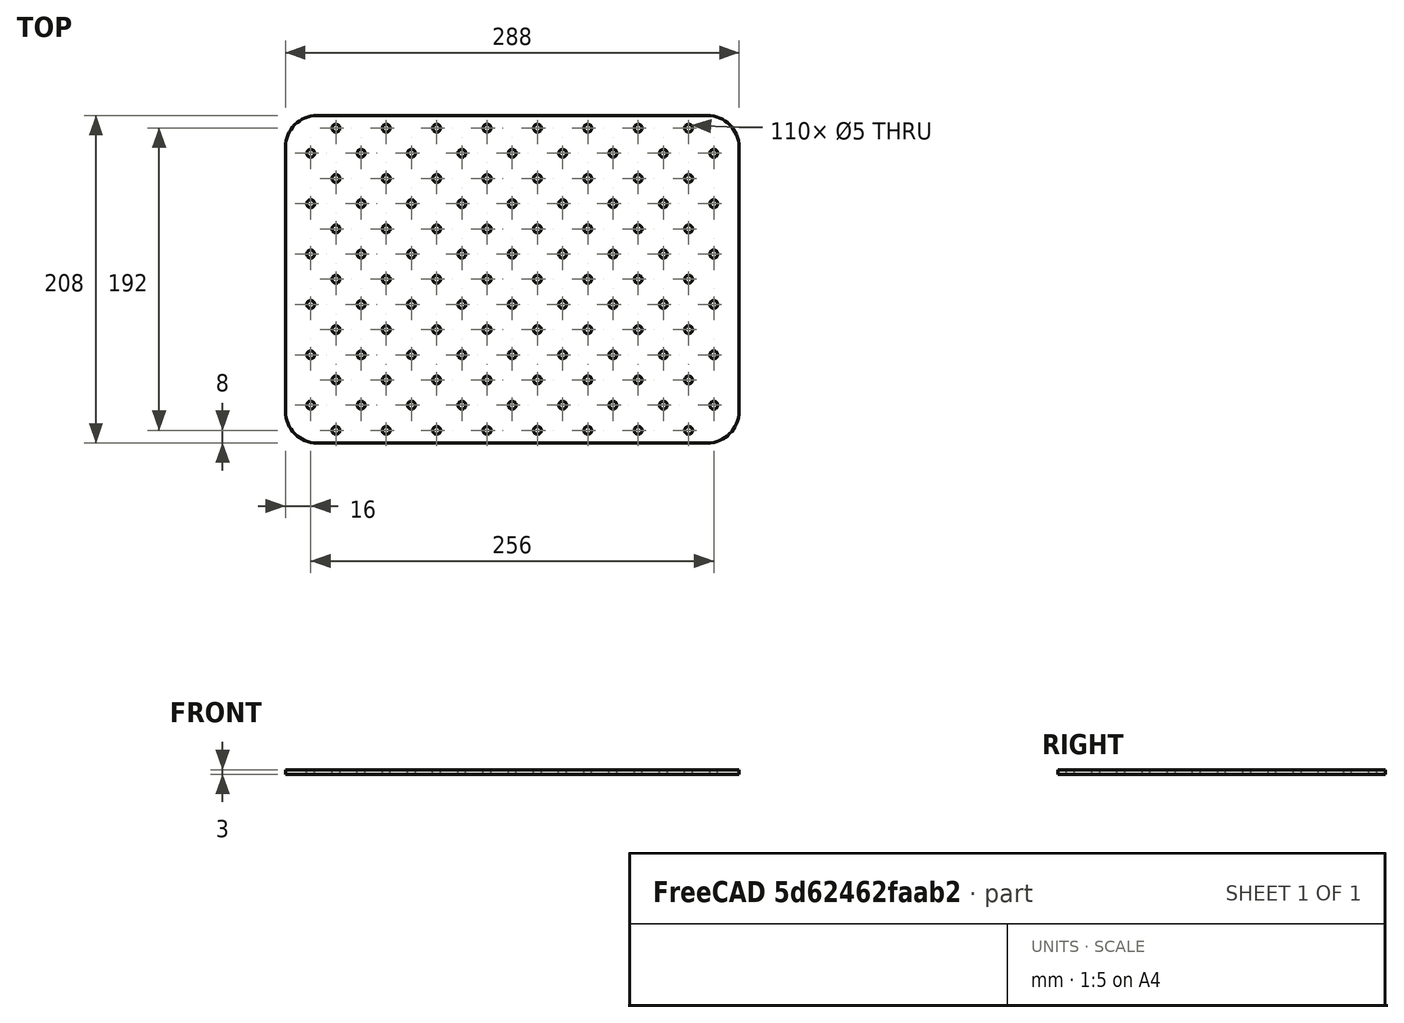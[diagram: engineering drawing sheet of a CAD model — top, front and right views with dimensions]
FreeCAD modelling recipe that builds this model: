
FCSTD DOCUMENT  (FreeCAD 0.21R33771 (Git))
Label: 32-grid-Base-Plate+16mm
License: All rights reserved
LicenseURL: http://en.wikipedia.org/wiki/All_rights_reserved
objects: TechDraw::DrawViewDimension×10, PartDesign::LinearPattern×4, Sketcher::SketchObject×3, TechDraw::DrawProjGroupItem×3, PartDesign::Hole×2, PartDesign::MultiTransform×2, TechDraw::DrawSVGTemplate×2, TechDraw::DrawPage×2, App::TextDocument×1, Spreadsheet::Sheet×1, PartDesign::Pad×1, TechDraw::DrawViewAnnotation×1, PartDesign::Body×1, TechDraw::DrawViewPart×1, TechDraw::DrawProjGroup×1, TechDraw::DrawViewBalloon×1
note: 34 computed .brp shape members not serialized (recipe doc carries the construction recipe); baked Part::Feature solids carry a one-line shape summary decoded from their .brp

FEATURE [Sketcher::SketchObject] Sketch  label="main-base-sketch"
  FullyConstrained = true
  MapMode = 5
  Support = -> [XY_Plane]
  expr: Constraints[16] = Spreadsheet.base_grid * Spreadsheet.vertical + Spreadsheet.extra_space
  expr: Constraints[17] = Spreadsheet.base_grid * Spreadsheet.horizontal
  expr: Constraints[18] = Spreadsheet.corner_rad
  sketch-geometry (8):
    g0: LineSegment StartX=-124 StartY=104 StartZ=0 EndX=124 EndY=104 EndZ=0
    g1: LineSegment StartX=144 StartY=84 StartZ=0 EndX=144 EndY=-84 EndZ=0
    g2: LineSegment StartX=124 StartY=-104 StartZ=0 EndX=-124 EndY=-104 EndZ=0
    g3: LineSegment StartX=-144 StartY=-84 StartZ=0 EndX=-144 EndY=84 EndZ=0
    g4: ArcOfCircle CenterX=124 CenterY=-84 CenterZ=0 NormalX=0 NormalY=0 NormalZ=1 AngleXU=0 Radius=20 StartAngle=4.71239 EndAngle=6.28319
    g5: ArcOfCircle CenterX=-124 CenterY=84 CenterZ=0 NormalX=0 NormalY=0 NormalZ=1 AngleXU=0 Radius=20 StartAngle=1.5708 EndAngle=3.14159
    g6: ArcOfCircle CenterX=124 CenterY=84 CenterZ=0 NormalX=0 NormalY=0 NormalZ=1 AngleXU=0 Radius=20 StartAngle=7e-16 EndAngle=1.5708
    g7: ArcOfCircle CenterX=-124 CenterY=-84 CenterZ=0 NormalX=0 NormalY=0 NormalZ=1 AngleXU=0 Radius=20 StartAngle=3.14159 EndAngle=4.71239
  constraints (19):
    c: Horizontal(g0)
    c: Horizontal(g2)
    c: Vertical(g1)
    c: Vertical(g3)
    c: Tangent(g1,g4) = 1.5708
    c: Tangent(g2,g4) = 1.5708
    c: Tangent(g3,g5) = 1.5708
    c: Tangent(g0,g5) = 1.5708
    c: Tangent(g0,g6) = 1.5708
    c: Tangent(g1,g6) = 1.5708
    c: Tangent(g3,g7) = 1.5708
    c: Tangent(g2,g7) = 1.5708
    c: Equal(g6,g4)
    c: Equal(g4,g7)
    c: Equal(g7,g5)
    c: Symmetric(g4,g5,g-1)
    c: DistanceY(g2,g0) = 208
    c: DistanceX(g3,g1) = 288
    c: Radius(g6) = 20
FEATURE [App::TextDocument] Text_document  label="notes"
  Text = 32mm+16mm Offset Double-Grid to be later transferred into different parametric options
FEATURE [Spreadsheet::Sheet] Spreadsheet  label="Parameters"
  cells = A1='Ref; B1='Value; C1='Description; A2='grid_boring; B2(grid_boring)=5; C2='main bore holes reference for grid; A3='corner_rad; B3(corner_rad)=20; C3='radius of the base plate corners; A4='base_grid; B4(base_grid)=32; C4='grid standard reference (standard 32mm); A5='thickness; B5(thickness)=3; C5='base plate thickness of material; A6='horizontal; B6(horizontal)=9; C6='holes horizonal; A7='vertical; B7(vertical)=6; C7='holes vertical; A8='grid_factor; B8(grid_factor)=1; C8='change the base grid reference for parametric designs; A9='extra_space; B9(extra_space)=16; C9='Extra Space vertically (Standard 0, Variant 16mm)
FEATURE [PartDesign::Pad] Pad
  Direction = (0,0,1)
  Length = 3
  Length2 = 10
  Profile = -> Sketch
  ReferenceAxis = -> Sketch [N_Axis]
  Type = 0
  expr: Length = Spreadsheet.thickness
FEATURE [Sketcher::SketchObject] Sketch001  label="bore-hole-sketch"
  FullyConstrained = true
  MapMode = 5
  Support = -> [XY_Plane]
  expr: Constraints[16] = Sketch.Constraints[16]
  expr: Constraints[17] = Sketch.Constraints[17]
  expr: Constraints[18] = Sketch.Constraints[18]
  expr: Constraints[19] = Spreadsheet.base_grid * Spreadsheet.grid_factor / 2 + Spreadsheet.extra_space / 2
  expr: Constraints[20] = Spreadsheet.base_grid * Spreadsheet.grid_factor / 2
  expr: Constraints[21] = Spreadsheet.grid_boring
  sketch-geometry (9):
    g0: LineSegment StartX=-124 StartY=104 StartZ=0 EndX=124 EndY=104 EndZ=0
    g1: LineSegment StartX=144 StartY=84 StartZ=0 EndX=144 EndY=-84 EndZ=0
    g2: LineSegment StartX=124 StartY=-104 StartZ=0 EndX=-124 EndY=-104 EndZ=0
    g3: LineSegment StartX=-144 StartY=-84 StartZ=0 EndX=-144 EndY=84 EndZ=0
    g4: ArcOfCircle CenterX=124 CenterY=-84 CenterZ=0 NormalX=0 NormalY=0 NormalZ=1 AngleXU=0 Radius=20 StartAngle=4.71239 EndAngle=6.28319
    g5: ArcOfCircle CenterX=-124 CenterY=84 CenterZ=0 NormalX=0 NormalY=0 NormalZ=1 AngleXU=0 Radius=20 StartAngle=1.5708 EndAngle=3.14159
    g6: ArcOfCircle CenterX=124 CenterY=84 CenterZ=0 NormalX=0 NormalY=0 NormalZ=1 AngleXU=0 Radius=20 StartAngle=2e-16 EndAngle=1.5708
    g7: ArcOfCircle CenterX=-124 CenterY=-84 CenterZ=0 NormalX=0 NormalY=0 NormalZ=1 AngleXU=0 Radius=20 StartAngle=3.14159 EndAngle=4.71239
    g8: Circle CenterX=128 CenterY=80 CenterZ=0 NormalX=0 NormalY=0 NormalZ=1 AngleXU=0 Radius=2.5
  constraints (22):
    c: Horizontal(g0)
    c: Horizontal(g2)
    c: Vertical(g1)
    c: Vertical(g3)
    c: Tangent(g1,g4) = 1.5708
    c: Tangent(g2,g4) = 1.5708
    c: Tangent(g3,g5) = 1.5708
    c: Tangent(g0,g5) = 1.5708
    c: Tangent(g0,g6) = 1.5708
    c: Tangent(g1,g6) = 1.5708
    c: Tangent(g3,g7) = 1.5708
    c: Tangent(g2,g7) = 1.5708
    c: Equal(g6,g4)
    c: Equal(g4,g7)
    c: Equal(g7,g5)
    c: Symmetric(g4,g5,g-1)
    c: DistanceY(g2,g0) = 208
    c: DistanceX(g3,g1) = 288
    c: Radius(g6) = 20
    c: DistanceY(g8,g0) = 24
    c: DistanceX(g8,g1) = 16
    c: Diameter(g8) = 5
FEATURE [PartDesign::Hole] Hole  label="Base-Bore-Hole"
  BaseFeature = -> Pad
  CustomThreadClearance = 0
  Depth = 699.261
  DepthType = 1
  Diameter = 5
  DrillForDepth = false
  DrillPoint = 1
  DrillPointAngle = 118
  HoleCutCountersinkAngle = 90
  HoleCutCustomValues = false
  HoleCutDepth = 0
  HoleCutDiameter = 6.1
  HoleCutType = 0
  ModelThread = false
  Profile = -> Sketch001
  Reversed = true
  Tapered = false
  TaperedAngle = 90
  ThreadClass = 0
  ThreadDepth = 699.261
  ThreadDepthType = 0
  ThreadDirection = 0
  ThreadFit = 0
  ThreadSize = 0
  ThreadType = 0
  Threaded = false
  UseCustomThreadClearance = false
  expr: Diameter = Spreadsheet.grid_boring
FEATURE [PartDesign::LinearPattern] LinearPattern
  Direction = -> Sketch001 [H_Axis]
  Length = 256
  Occurrences = 9
  Reversed = true
  expr: Length = Spreadsheet.base_grid * Spreadsheet.grid_factor * (Spreadsheet.horizontal / Spreadsheet.grid_factor - 1)
  expr: Occurrences = Spreadsheet.horizontal / Spreadsheet.grid_factor
FEATURE [PartDesign::LinearPattern] LinearPattern001
  Direction = -> Sketch001 [V_Axis]
  Length = 160
  Occurrences = 6
  Reversed = true
  expr: Length = Spreadsheet.base_grid * Spreadsheet.grid_factor * (Spreadsheet.vertical / Spreadsheet.grid_factor - 1)
  expr: Occurrences = Spreadsheet.vertical / Spreadsheet.grid_factor
FEATURE [PartDesign::MultiTransform] MultiTransform  label="Base-Grid-Bore-Holes"
  BaseFeature = -> Hole
  Originals = -> [Hole]
  Transformations = -> [LinearPattern,LinearPattern001]
FEATURE [TechDraw::DrawSVGTemplate] Template001  label="Base Plate Page1"
  EditableTexts = AUTHOR_NAME=Timm Wille; DRAWING_TITLE=32mmx2 (+16mm) Grid Base Plate; FC-DATE=16.10.2024; FC-REV=v0.2-1; FC-SC=1/2; FC-SH=1 / 1; FC-SI=A3; FreeCAD_DRAWING=FreeCAD DRAWING; SI-1=in mm; SI-6=LICENSE: CC-BY-SA 4.0
  Height = 297
  Orientation = 1
  Template = <path>
  Width = 420
FEATURE [TechDraw::DrawSVGTemplate] Template
  Height = 297
  Orientation = 1
  Template = <path>
  Width = 420
FEATURE [Sketcher::SketchObject] Sketch002  label="secondary-grid-bore-hole"
  ExternalGeometry = -> [Sketch001,Sketch]
  FullyConstrained = true
  MapMode = 5
  Support = -> [XY_Plane]
  expr: Constraints[0] = Spreadsheet.base_grid / 2
  expr: Constraints[1] = Spreadsheet.base_grid / 2
  expr: Constraints[2] = Spreadsheet.grid_boring
  sketch-geometry (1):
    g0: Circle CenterX=112 CenterY=96 CenterZ=0 NormalX=0 NormalY=0 NormalZ=1 AngleXU=0 Radius=2.5
  constraints (3):
    c: DistanceX(g0,g-3) = 16
    c: DistanceY(g-3,g0) = 16
    c: Diameter(g0) = 5
FEATURE [TechDraw::DrawViewAnnotation] Annotation
  Font = osifont
  LineSpace = 100
  LockPosition = false
  MaxWidth = -1
  Rotation = 0
  ScaleType = 0
  Text = Technical Drawing of the #ASKotec Modules Base Plate | 2x 32x32mm grid paddern (shift 16mm) for Prototyping | packing and collections setups
  TextSize = 5
  TextStyle = 0
  X = 120.347
  Y = 202.608
FEATURE [PartDesign::Hole] Hole001  label="Secondary-Bore-Hole"
  BaseFeature = -> MultiTransform
  CustomThreadClearance = 0
  Depth = 717.646
  DepthType = 1
  Diameter = 5
  DrillForDepth = false
  DrillPoint = 1
  DrillPointAngle = 118
  HoleCutCountersinkAngle = 90
  HoleCutCustomValues = false
  HoleCutDepth = 0
  HoleCutDiameter = 6.1
  HoleCutType = 0
  ModelThread = false
  Profile = -> Sketch002
  Reversed = true
  Tapered = false
  TaperedAngle = 90
  ThreadClass = 0
  ThreadDepth = 717.646
  ThreadDepthType = 0
  ThreadDirection = 0
  ThreadFit = 0
  ThreadSize = 0
  ThreadType = 0
  Threaded = false
  UseCustomThreadClearance = false
  expr: Diameter = Spreadsheet.grid_boring
FEATURE [PartDesign::LinearPattern] LinearPattern002
  Direction = -> Sketch002 [H_Axis]
  Length = 224
  Occurrences = 8
  Reversed = true
  expr: Length = Spreadsheet.base_grid * Spreadsheet.grid_factor * (Spreadsheet.horizontal / Spreadsheet.grid_factor - 2)
  expr: Occurrences = Spreadsheet.horizontal - 1
FEATURE [PartDesign::LinearPattern] LinearPattern003
  Direction = -> Sketch002 [V_Axis]
  Length = 192
  Occurrences = 7
  Reversed = true
  expr: Length = Spreadsheet.base_grid * Spreadsheet.grid_factor * Spreadsheet.vertical / Spreadsheet.grid_factor
  expr: Occurrences = Spreadsheet.vertical + 1
FEATURE [PartDesign::MultiTransform] MultiTransform001  label="Secondary-Grid-Bore-Holes"
  BaseFeature = -> Hole001
  Originals = -> [Hole001]
  Transformations = -> [LinearPattern002,LinearPattern003]
FEATURE [PartDesign::Body] Body  label="Base-Plate"
  Group = -> [Sketch,Pad,Sketch001,Hole,MultiTransform,LinearPattern,LinearPattern001,Sketch002,Hole001,MultiTransform001,LinearPattern002,LinearPattern003]
  Origin = -> Origin
  Tip = -> MultiTransform001
FEATURE [TechDraw::DrawProjGroupItem] ProjItem  label="Front"
  CoarseView = false
  Direction = (0,-1,0)
  Focus = 100
  HardHidden = false
  IsoCount = 0
  IsoHidden = false
  IsoVisible = false
  LockPosition = true
  Perspective = false
  Rotation = 0
  RotationVector = (1,0,0)
  Scale = 0.5
  ScaleType = 2
  ScrubCount = 0
  SeamHidden = false
  SeamVisible = false
  SmoothHidden = false
  SmoothVisible = true
  Source = -> [Body]
  Type = 0
  X = 0
  XDirection = (-1,0,1e-16)
  Y = 0
FEATURE [TechDraw::DrawProjGroupItem] ProjItem002  label="FrontTopRight"
  CoarseView = false
  Direction = (-0.57735,-0.57735,-0.57735)
  Focus = 100
  HardHidden = false
  IsoCount = 0
  IsoHidden = false
  IsoVisible = false
  LockPosition = true
  Perspective = false
  Rotation = 0
  RotationVector = (1,0,0)
  ScaleType = 2
  ScrubCount = 0
  SeamHidden = false
  SeamVisible = false
  SmoothHidden = false
  SmoothVisible = true
  Source = -> [Body]
  Type = 7
  X = -176.645
  XDirection = (-0.707107,0.707107,1e-16)
  Y = -177.1
FEATURE [TechDraw::DrawViewDimension] Dimension002
  AngleOverride = false
  Arbitrary = false
  ArbitraryTolerances = false
  EqualTolerance = true
  ExtensionAngle = 0
  FormatSpec = %.2w
  FormatSpecOverTolerance = %+.2w
  FormatSpecUnderTolerance = %+.2w
  Inverted = false
  LineAngle = 0
  LockPosition = false
  MeasureType = 1
  OverTolerance = 0
  References2D = -> [ProjItem]
  Rotation = 0
  ScaleType = 0
  TheoreticalExact = false
  Type = 2
  UnderTolerance = 0
  X = 79.6749
  Y = 11.0925
FEATURE [TechDraw::DrawViewPart] View
  CoarseView = false
  Direction = (0,0,1)
  Focus = 100
  HardHidden = false
  IsoCount = 0
  IsoHidden = false
  IsoVisible = false
  LockPosition = false
  Perspective = false
  Rotation = 0
  ScaleType = 0
  ScrubCount = 0
  SeamHidden = false
  SeamVisible = false
  SmoothHidden = false
  SmoothVisible = true
  Source = -> [Body]
  X = 217.568
  XDirection = (1,0,0)
  Y = 155.059
FEATURE [TechDraw::DrawPage] Page  label="2D SVG Export"
  KeepUpdated = true
  NextBalloonIndex = 1
  ProjectionType = 0
  Template = -> Template
  Views = -> [View]
FEATURE [TechDraw::DrawProjGroupItem] ProjItem001  label="Top"
  CoarseView = false
  Direction = (-1e-16,0,-1)
  Focus = 100
  HardHidden = false
  IsoCount = 0
  IsoHidden = false
  IsoVisible = false
  LockPosition = false
  Perspective = false
  Rotation = 0
  RotationVector = (1,0,0)
  Scale = 0.5
  ScaleType = 2
  ScrubCount = 0
  SeamHidden = false
  SeamVisible = false
  SmoothHidden = false
  SmoothVisible = true
  Source = -> [Body]
  Type = 4
  X = 0
  XDirection = (-1,0,1e-16)
  Y = -67.75
FEATURE [TechDraw::DrawProjGroup] ProjGroup
  Anchor = -> ProjItem
  AutoDistribute = true
  LockPosition = false
  ProjectionType = 0
  Rotation = 0
  Scale = 0.5
  ScaleType = 2
  Source = -> [Body]
  Views = -> [ProjItem,ProjItem001,ProjItem002]
  X = 301.061
  Y = 257.02
  spacingX = 15
  spacingY = 15
FEATURE [TechDraw::DrawViewDimension] Dimension
  AngleOverride = false
  Arbitrary = false
  ArbitraryTolerances = false
  EqualTolerance = true
  ExtensionAngle = 0
  FormatSpec = %.2w
  FormatSpecOverTolerance = %+.2w
  FormatSpecUnderTolerance = %+.2w
  Inverted = false
  LineAngle = 0
  LockPosition = false
  MeasureType = 1
  OverTolerance = 0
  References2D = -> [ProjItem001]
  Rotation = 0
  ScaleType = 0
  TheoreticalExact = false
  Type = 1
  UnderTolerance = 0
  X = -0.47588
  Y = -74.1283
FEATURE [TechDraw::DrawViewDimension] Dimension004
  AngleOverride = false
  Arbitrary = false
  ArbitraryTolerances = false
  EqualTolerance = true
  ExtensionAngle = 0
  FormatSpec = R%.2w
  FormatSpecOverTolerance = %+.2w
  FormatSpecUnderTolerance = %+.2w
  Inverted = false
  LineAngle = 0
  LockPosition = false
  MeasureType = 1
  OverTolerance = 0
  References2D = -> [ProjItem001]
  Rotation = 0
  ScaleType = 0
  TheoreticalExact = false
  Type = 4
  UnderTolerance = 0
  X = 88.321
  Y = -60.3052
FEATURE [TechDraw::DrawViewBalloon] Balloon
  BubbleShape = 6
  EndType = 0
  EndTypeScale = 1
  KinkLength = 5
  LockPosition = false
  OriginX = -102.96
  OriginY = -87.5189
  Rotation = 0
  ScaleType = 0
  ShapeScale = 1
  SourceView = -> ProjItem001
  Text = 2x32x32mm by 16mm shifted bore holes grid paddern
  TextWrapLen = -1
  X = 35.9411
  Y = -208.188
FEATURE [TechDraw::DrawViewDimension] Dimension005
  AngleOverride = false
  Arbitrary = false
  ArbitraryTolerances = false
  EqualTolerance = true
  ExtensionAngle = 0
  FormatSpec = %.2w
  FormatSpecOverTolerance = %+.2w
  FormatSpecUnderTolerance = %+.2w
  Inverted = false
  LineAngle = 0
  LockPosition = false
  MeasureType = 1
  OverTolerance = 0
  References2D = -> [ProjItem001]
  Rotation = 0
  ScaleType = 0
  TheoreticalExact = false
  Type = 1
  UnderTolerance = 0
  X = -94.8606
  Y = 46.9272
FEATURE [TechDraw::DrawViewDimension] Dimension006
  AngleOverride = false
  Arbitrary = false
  ArbitraryTolerances = false
  EqualTolerance = true
  ExtensionAngle = 0
  FormatSpec = %.2w
  FormatSpecOverTolerance = %+.2w
  FormatSpecUnderTolerance = %+.2w
  Inverted = false
  LineAngle = 0
  LockPosition = false
  MeasureType = 1
  OverTolerance = 0
  References2D = -> [ProjItem001]
  Rotation = 0
  ScaleType = 0
  TheoreticalExact = false
  Type = 1
  UnderTolerance = 0
  X = -87.346
  Y = 61.872
FEATURE [TechDraw::DrawViewDimension] Dimension007
  AngleOverride = false
  Arbitrary = false
  ArbitraryTolerances = false
  EqualTolerance = true
  ExtensionAngle = 0
  FormatSpec = %.2w
  FormatSpecOverTolerance = %+.2w
  FormatSpecUnderTolerance = %+.2w
  Inverted = false
  LineAngle = 0
  LockPosition = false
  MeasureType = 1
  OverTolerance = 0
  References2D = -> [ProjItem001]
  Rotation = 0
  ScaleType = 0
  TheoreticalExact = false
  Type = 1
  UnderTolerance = 0
  X = -34.3443
  Y = 61.958
FEATURE [TechDraw::DrawViewDimension] Dimension008
  AngleOverride = false
  Arbitrary = false
  ArbitraryTolerances = false
  EqualTolerance = true
  ExtensionAngle = 0
  FormatSpec = %.2w
  FormatSpecOverTolerance = %+.2w
  FormatSpecUnderTolerance = %+.2w
  Inverted = false
  LineAngle = 0
  LockPosition = false
  MeasureType = 1
  OverTolerance = 0
  References2D = -> [ProjItem001]
  Rotation = 0
  ScaleType = 0
  TheoreticalExact = false
  Type = 2
  UnderTolerance = 0
  X = -88.4787
  Y = 24.8174
FEATURE [TechDraw::DrawViewDimension] Dimension009
  AngleOverride = false
  Arbitrary = false
  ArbitraryTolerances = false
  EqualTolerance = true
  ExtensionAngle = 0
  FormatSpec = %.2w
  FormatSpecOverTolerance = %+.2w
  FormatSpecUnderTolerance = %+.2w
  Inverted = false
  LineAngle = 0
  LockPosition = false
  MeasureType = 1
  OverTolerance = 0
  References2D = -> [ProjItem001]
  Rotation = 0
  ScaleType = 0
  TheoreticalExact = false
  Type = 2
  UnderTolerance = 0
  X = -83.2417
  Y = 3.43234
FEATURE [TechDraw::DrawViewDimension] Dimension010
  AngleOverride = false
  Arbitrary = false
  ArbitraryTolerances = false
  EqualTolerance = true
  ExtensionAngle = 0
  FormatSpec = ⌀%.2w
  FormatSpecOverTolerance = %+.2w
  FormatSpecUnderTolerance = %+.2w
  Inverted = false
  LineAngle = 0
  LockPosition = false
  MeasureType = 1
  OverTolerance = 0
  References2D = -> [ProjItem001]
  Rotation = 0
  ScaleType = 0
  TheoreticalExact = false
  Type = 5
  UnderTolerance = 0
  X = -90.0169
  Y = -28.5768
FEATURE [TechDraw::DrawViewDimension] Dimension011
  AngleOverride = false
  Arbitrary = false
  ArbitraryTolerances = false
  EqualTolerance = true
  ExtensionAngle = 0
  FormatSpec = %.2w
  FormatSpecOverTolerance = %+.2w
  FormatSpecUnderTolerance = %+.2w
  Inverted = false
  LineAngle = 0
  LockPosition = false
  MeasureType = 1
  OverTolerance = 0
  References2D = -> [ProjItem001]
  Rotation = 0
  ScaleType = 0
  TheoreticalExact = false
  Type = 2
  UnderTolerance = 0
  X = 87.3026
  Y = -22.1512
FEATURE [TechDraw::DrawPage] Page001  label="A3-Technical Drawing"
  KeepUpdated = true
  NextBalloonIndex = 3
  ProjectionType = 0
  Template = -> Template001
  Views = -> [ProjGroup,Dimension,Dimension002,Dimension004,Balloon,Annotation,Dimension005,Dimension006,Dimension007,Dimension008,Dimension009,Dimension010,Dimension011]
note: 2 file-system paths scrubbed to <path> (originals preserved in the JSON sidecar)
